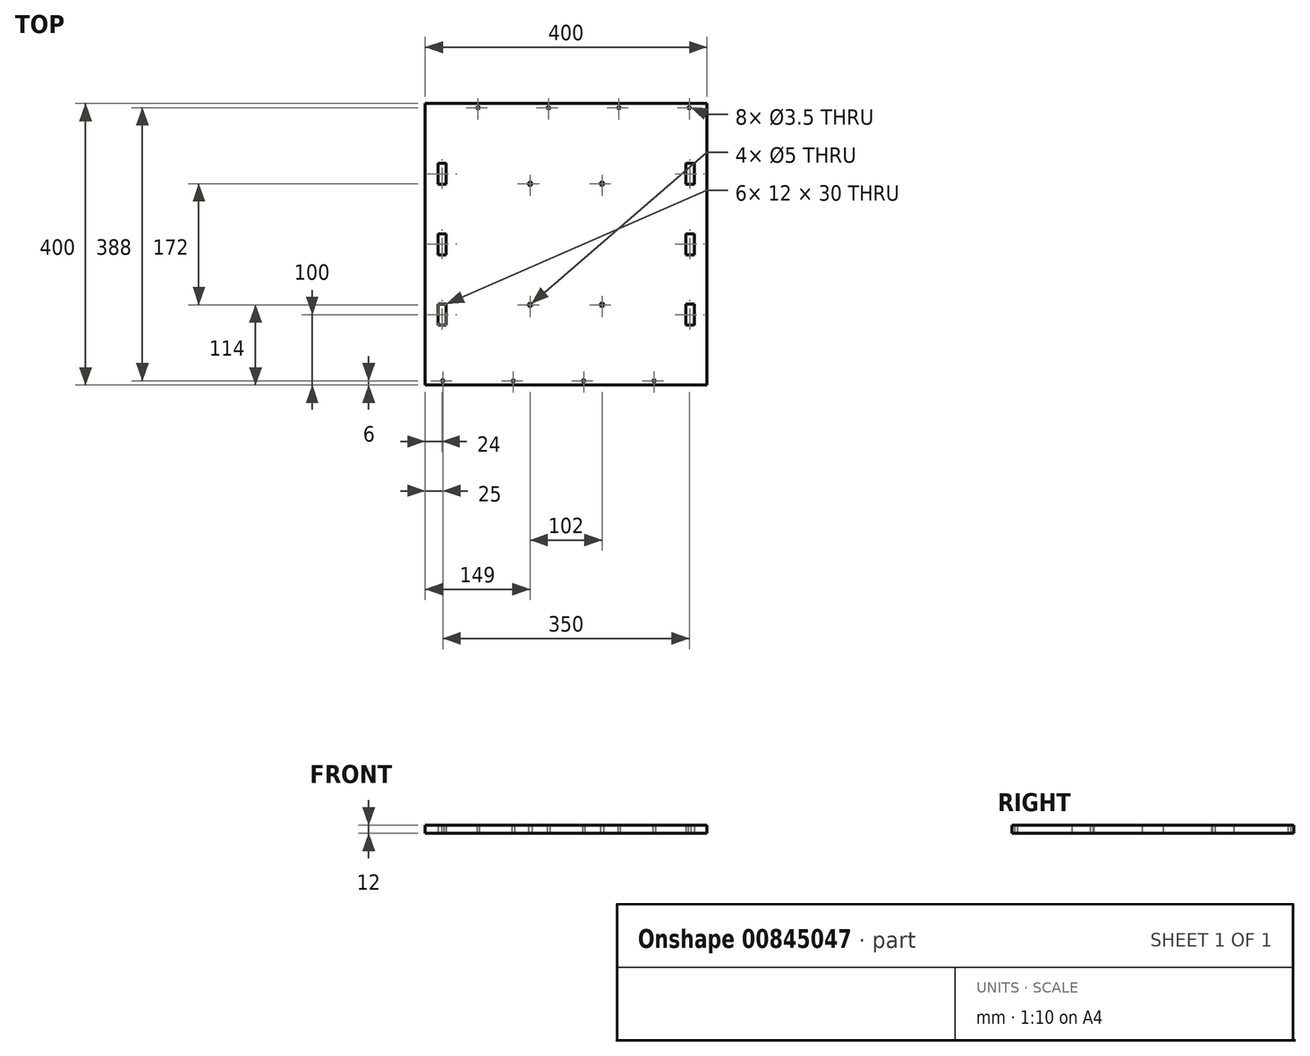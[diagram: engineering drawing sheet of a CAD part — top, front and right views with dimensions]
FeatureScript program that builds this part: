
annotation { "Feature Type Name" : "Feature", "Feature Type Description" : "" }
export const myFeature = defineFeature(function(context is Context, id is Id, definition is map)
    precondition{}
    {
        {
            var Q0;
            Q0=qCreatedBy(makeId("Top.planeOp"),FACE);
            var sketch = newSketch(context, id + "F0", { "sketchPlane" : qUnion([Q0])});
            skLineSegment(sketch, "E0.bottom", {"start": v(0, 0) * mm, "end": v(400, 0) * mm});
            skLineSegment(sketch, "E0.top", {"start": v(0, 400) * mm, "end": v(400, 400) * mm});
            skLineSegment(sketch, "E0.left", {"start": v(0, 0) * mm, "end": v(0, 400) * mm});
            skLineSegment(sketch, "E0.right", {"start": v(400, 0) * mm, "end": v(400, 400) * mm});
            skCircle(sketch, "E1", {"center": v(75, 394) * mm, "radius": 1.75 * mm});
            skCircle(sketch, "E2", {"center": v(175, 394) * mm, "radius": 1.75 * mm});
            skCircle(sketch, "E3", {"center": v(275, 394) * mm, "radius": 1.75 * mm});
            skCircle(sketch, "E4", {"center": v(375, 394) * mm, "radius": 1.75 * mm});
            skCircle(sketch, "E5", {"center": v(25, 6) * mm, "radius": 1.75 * mm});
            skCircle(sketch, "E6", {"center": v(125, 6) * mm, "radius": 1.75 * mm});
            skCircle(sketch, "E7", {"center": v(225, 6) * mm, "radius": 1.75 * mm});
            skCircle(sketch, "E8", {"center": v(325, 6) * mm, "radius": 1.75 * mm});
            skLineSegment(sketch, "E9.bottom", {"start": v(30, 85) * mm, "end": v(18, 85) * mm});
            skLineSegment(sketch, "E9.top", {"start": v(30, 115) * mm, "end": v(18, 115) * mm});
            skLineSegment(sketch, "E9.left", {"start": v(30, 85) * mm, "end": v(30, 115) * mm});
            skLineSegment(sketch, "E9.right", {"start": v(18, 85) * mm, "end": v(18, 115) * mm});
            skPoint(sketch, "E9.middle", {"position": v(24, 100) * mm});
            skLineSegment(sketch, "E10.bottom", {"start": v(30, 285) * mm, "end": v(18, 285) * mm});
            skLineSegment(sketch, "E10.top", {"start": v(30, 315) * mm, "end": v(18, 315) * mm});
            skLineSegment(sketch, "E10.left", {"start": v(30, 285) * mm, "end": v(30, 315) * mm});
            skLineSegment(sketch, "E10.right", {"start": v(18, 285) * mm, "end": v(18, 315) * mm});
            skPoint(sketch, "E10.middle", {"position": v(24, 300) * mm});
            skLineSegment(sketch, "E11.bottom", {"start": v(30, 185) * mm, "end": v(18, 185) * mm});
            skLineSegment(sketch, "E11.top", {"start": v(30, 215) * mm, "end": v(18, 215) * mm});
            skLineSegment(sketch, "E11.left", {"start": v(30, 185) * mm, "end": v(30, 215) * mm});
            skLineSegment(sketch, "E11.right", {"start": v(18, 185) * mm, "end": v(18, 215) * mm});
            skPoint(sketch, "E11.middle", {"position": v(24, 200) * mm});
            skLineSegment(sketch, "E12.bottom", {"start": v(370, 185) * mm, "end": v(382, 185) * mm});
            skLineSegment(sketch, "E12.top", {"start": v(370, 215) * mm, "end": v(382, 215) * mm});
            skLineSegment(sketch, "E12.left", {"start": v(370, 185) * mm, "end": v(370, 215) * mm});
            skLineSegment(sketch, "E12.right", {"start": v(382, 185) * mm, "end": v(382, 215) * mm});
            skPoint(sketch, "E12.middle", {"position": v(376, 200) * mm});
            skLineSegment(sketch, "E13.bottom", {"start": v(382, 85) * mm, "end": v(370, 85) * mm});
            skLineSegment(sketch, "E13.top", {"start": v(382, 115) * mm, "end": v(370, 115) * mm});
            skLineSegment(sketch, "E13.left", {"start": v(382, 85) * mm, "end": v(382, 115) * mm});
            skLineSegment(sketch, "E13.right", {"start": v(370, 85) * mm, "end": v(370, 115) * mm});
            skPoint(sketch, "E13.middle", {"position": v(376, 100) * mm});
            skLineSegment(sketch, "E14.bottom", {"start": v(382, 285) * mm, "end": v(370, 285) * mm});
            skLineSegment(sketch, "E14.top", {"start": v(382, 315) * mm, "end": v(370, 315) * mm});
            skLineSegment(sketch, "E14.left", {"start": v(382, 285) * mm, "end": v(382, 315) * mm});
            skLineSegment(sketch, "E14.right", {"start": v(370, 285) * mm, "end": v(370, 315) * mm});
            skPoint(sketch, "E14.middle", {"position": v(376, 300) * mm});
            skCircle(sketch, "E15", {"center": v(149, 286) * mm, "radius": 2.5 * mm});
            skCircle(sketch, "E16", {"center": v(251, 286) * mm, "radius": 2.5 * mm});
            skCircle(sketch, "E17", {"center": v(149, 114) * mm, "radius": 2.5 * mm});
            skCircle(sketch, "E18", {"center": v(251, 114) * mm, "radius": 2.5 * mm});
            skSolve(sketch);
        }
        {
            var Q0;
            Q0=makeQuery(id+"F0.imprint","IMPRINT",FACE,{"disambiguationData":[TD([[makeQuery(id+"F0.imprint","IMPRINT",EDGE,{"derivedFrom":sQuery(id+"F0.wireOp",EDGE,"E0.bottom")}),1.0]])]});
            extrude(context, id + "F1", {"entities" : qUnion([Q0]), "depth" : 12 * mm, "offsetDistance" : 25 * mm});
        }
    });
